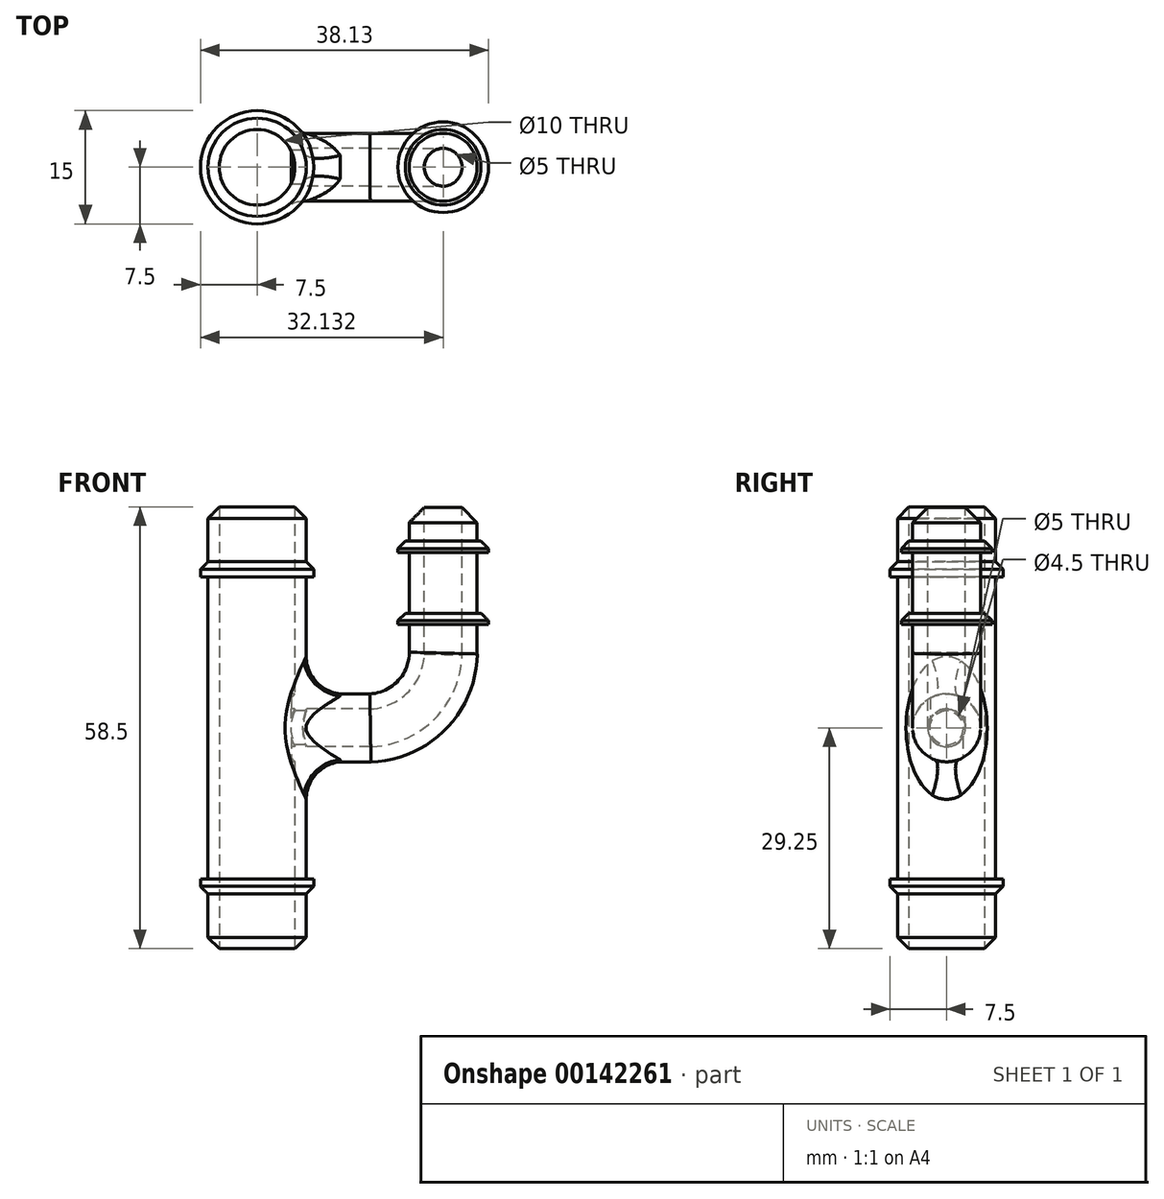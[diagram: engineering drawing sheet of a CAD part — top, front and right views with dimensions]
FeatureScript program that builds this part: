
annotation { "Feature Type Name" : "Feature", "Feature Type Description" : "" }
export const myFeature = defineFeature(function(context is Context, id is Id, definition is map)
    precondition{}
    {
        {
            var Q0;
            Q0=qCreatedBy(makeId("Front.planeOp"),FACE);
            var sketch = newSketch(context, id + "F0", { "sketchPlane" : qUnion([Q0])});
            skLineSegment(sketch, "E0.bottom", {"start": v(4.5, 4.5) * mm, "end": v(34.5, 4.5) * mm});
            skLineSegment(sketch, "E0.top", {"start": v(4.5, 2.5) * mm, "end": v(11, 2.5) * mm});
            skLineSegment(sketch, "E0.left", {"start": v(4.5, 4.5) * mm, "end": v(4.5, 2.5) * mm});
            skLineSegment(sketch, "E0.right", {"start": v(11, 4.5) * mm, "end": v(11, 2.5) * mm});
            skLineSegment(sketch, "E1", {"start": v(-36.5, 0) * mm, "end": v(54.36, 0) * mm, "construction": true});
            skLineSegment(sketch, "E2", {"start": v(0, 12.73) * mm, "end": v(0, -11.94) * mm, "construction": true});
            skSolve(sketch);
        }
        {
            var Q0;
            Q0=makeQuery(id+"F0.imprint","IMPRINT",FACE,{"disambiguationData":[TD([[makeQuery(id+"F0.imprint","IMPRINT",EDGE,{"derivedFrom":sQuery(id+"F0.wireOp",EDGE,"E0.bottom")}),-1.0]])]});
            var Q1;
            {var subQ0=sQuery(id+"F0.wireOp",EDGE,"a35777e7-ca00-45c0-8781-a7bbb4af3e560.MirrorCS");Q1=makeQuery(id+"F0.imprint","IMPRINT",FACE,{"disambiguationData":[TD([[makeQuery(id+"F0.imprint","IMPRINT",EDGE,{"derivedFrom":subQ0}),-1.0]])]});}
            var Q2;
            Q2=makeQuery(id+"F0.imprint","IMPRINT",FACE,{"disambiguationData":[TD([[makeQuery(id+"F0.imprint","IMPRINT",EDGE,{"derivedFrom":sQuery(id+"F0.wireOp",EDGE,"mlNMObRF-hjKZ-VAvK-cDcy-euMoUcQcRU43.bottom")}),-1.0]])]});
            var Q3;
            Q3=sQuery(id+"F0.wireOp",EDGE,"E1");
            revolve(context, id + "F1", {"entities" : qUnion([Q0, Q1, Q2]), "axis" : qUnion([Q3]), "revolveType" : RevolveType.FULL});
        }
        {
            var Q0;
            Q0=qCreatedBy(makeId("Top.planeOp"),FACE);
            var sketch = newSketch(context, id + "F2", { "sketchPlane" : qUnion([Q0])});
            skCircle(sketch, "E3", {"center": v(0, 0) * mm, "radius": 6.5 * mm});
            skCircle(sketch, "E4", {"center": v(0, 0) * mm, "radius": 5 * mm});
            skSolve(sketch);
        }
        {
            var Q0;
            Q0=makeQuery(id+"F2.imprint","IMPRINT",FACE,{"disambiguationData":[TD([[makeQuery(id+"F2.imprint","IMPRINT",EDGE,{"derivedFrom":sQuery(id+"F2.wireOp",EDGE,"E3")}),1.0]])]});
            extrude(context, id + "F3", {"entities" : qUnion([Q0]), "operationType" : NewBodyOperationType.ADD, "endBound" : BoundingType.SYMMETRIC, "depth" : 61.5 * mm});
        }
        {
            var Q0;
            Q0=makeQuery(id+"F3.opExtrude","CAP_EDGE",EDGE,{"disambiguationData":[OSD([sQuery(id+"F2.wireOp",EDGE,"E3")])],"isStart":false});
            var Q1;
            Q1=makeQuery(id+"F3.opExtrude","CAP_EDGE",EDGE,{"disambiguationData":[OSD([sQuery(id+"F2.wireOp",EDGE,"E3")])],"isStart":true});
            chamfer(context, id + "F4", {"entities" : qUnion([Q0, Q1]), "width" : 3 * mm, "tangentPropagation" : true});
        }
        {
            var Q0;
            {var subQ0=sQuery(id+"F0.wireOp",EDGE,"E0.bottom");Q0=makeQuery(id+"F3.boolean.opBoolean","INTERSECT",EDGE,{"derivedFrom":[makeQuery(id+"F1.opRevolve","SWEPT_FACE",FACE,{"disambiguationData":[OSD([subQ0]),TDD([makeQuery(id+"F0.imprint","IMPRINT",EDGE,{"disambiguationData":[TD([[makeQuery(id+"F0.imprint","INTERSECT",VERTEX,{"derivedFrom":[subQ0,sQuery(id+"F0.wireOp",EDGE,"E0.left")]}),-1.0]])],"derivedFrom":subQ0})])]}),makeQuery(id+"F3.opExtrude","SWEPT_FACE",FACE,{"disambiguationData":[OSD([sQuery(id+"F2.wireOp",EDGE,"E3")])]})]});}
            fillet(context, id + "F5", {"entities" : qUnion([Q0]), "radius" : 5 * mm, "tangentPropagation" : true, "allowEdgeOverflow" : false});
        }
        {
            var Q0;
            Q0=qCreatedBy(makeId("Front.planeOp"),FACE);
            var sketch = newSketch(context, id + "F6", { "sketchPlane" : qUnion([Q0])});
            skLineSegment(sketch, "E5", {"start": v(0, 31.28) * mm, "end": v(0, -33.3) * mm, "construction": true});
            skLineSegment(sketch, "E6.bottom", {"start": v(-7.5, 22) * mm, "end": v(-5.5, 22) * mm});
            skLineSegment(sketch, "E6.top", {"start": v(-7.5, 20) * mm, "end": v(-5.5, 20) * mm});
            skLineSegment(sketch, "E6.left", {"start": v(-7.5, 22) * mm, "end": v(-7.5, 20) * mm});
            skLineSegment(sketch, "E6.right", {"start": v(-5.5, 22) * mm, "end": v(-5.5, 20) * mm});
            skLineSegment(sketch, "E7", {"start": v(-17.18, 0) * mm, "end": v(34.4, 0) * mm, "construction": true});
            skLineSegment(sketch, "E8.MirrorCS", {"start": v(-7.5, -22) * mm, "end": v(-7.5, -20) * mm});
            skLineSegment(sketch, "E9.MirrorCS", {"start": v(-7.5, -22) * mm, "end": v(-5.5, -22) * mm});
            skLineSegment(sketch, "E10.MirrorCS", {"start": v(-5.5, -22) * mm, "end": v(-5.5, -20) * mm});
            skLineSegment(sketch, "E11.MirrorCS", {"start": v(-7.5, -20) * mm, "end": v(-5.5, -20) * mm});
            skSolve(sketch);
        }
        {
            var Q0;
            Q0=makeQuery(id+"F6.imprint","IMPRINT",FACE,{"disambiguationData":[TD([[makeQuery(id+"F6.imprint","IMPRINT",EDGE,{"derivedFrom":sQuery(id+"F6.wireOp",EDGE,"E6.bottom")}),-1.0]])]});
            var Q1;
            Q1=makeQuery(id+"F6.imprint","IMPRINT",FACE,{"disambiguationData":[TD([[makeQuery(id+"F6.imprint","IMPRINT",EDGE,{"derivedFrom":sQuery(id+"F6.wireOp",EDGE,"E8.MirrorCS")}),-1.0]])]});
            var Q2;
            Q2=sQuery(id+"F6.wireOp",EDGE,"E5");
            revolve(context, id + "F7", {"operationType" : NewBodyOperationType.ADD, "entities" : qUnion([Q0, Q1]), "axis" : qUnion([Q2]), "revolveType" : RevolveType.FULL});
        }
        {
            var Q0;
            Q0=makeQuery(id+"F7.opRevolve","SWEPT_EDGE",EDGE,{"disambiguationData":[OSD([sQuery(id+"F6.wireOp",EDGE,"E8.MirrorCS"),sQuery(id+"F6.wireOp",EDGE,"E9.MirrorCS")])]});
            var Q1;
            Q1=makeQuery(id+"F7.opRevolve","SWEPT_EDGE",EDGE,{"disambiguationData":[OSD([sQuery(id+"F6.wireOp",EDGE,"E6.bottom"),sQuery(id+"F6.wireOp",EDGE,"E6.left")])]});
            chamfer(context, id + "F8", {"entities" : qUnion([Q0, Q1]), "width" : 1 * mm, "tangentPropagation" : true});
        }
        {
            var Q0;
            Q0=qCreatedBy(makeId("Right.planeOp"),FACE);
            var sketch = newSketch(context, id + "F9", { "sketchPlane" : qUnion([Q0])});
            skCircle(sketch, "E12", {"center": v(0, 0) * mm, "radius": 2.25 * mm});
            skSolve(sketch);
        }
        {
            var Q0;
            Q0=makeQuery(id+"F9.imprint","IMPRINT",FACE,{"disambiguationData":[TD([[makeQuery(id+"F9.imprint","IMPRINT",EDGE,{"derivedFrom":sQuery(id+"F9.wireOp",EDGE,"E12")}),1.0]])]});
            extrude(context, id + "F10", {"entities" : qUnion([Q0]), "operationType" : NewBodyOperationType.REMOVE, "depth" : 10 * mm});
        }
        {
            var Q0;
            Q0=qCreatedBy(makeId("Front.planeOp"),FACE);
            var sketch = newSketch(context, id + "F11", { "sketchPlane" : qUnion([Q0])});
            skLineSegment(sketch, "E13", {"start": v(11.05, 0) * mm, "end": v(15, 0) * mm});
            skLineSegment(sketch, "E14", {"start": v(24.63, 9.73) * mm, "end": v(24.63, 29.73) * mm});
            skArc(sketch, "E15", {"start": v(15, 0) * mm, "mid": v(21.74, 2.96) * mm, "end": v(24.63, 9.73) * mm});
            skLineSegment(sketch, "E16.bottom", {"start": v(18.63, 24.73) * mm, "end": v(20.13, 24.73) * mm});
            skLineSegment(sketch, "E16.top", {"start": v(18.63, 23.23) * mm, "end": v(20.13, 23.23) * mm});
            skLineSegment(sketch, "E16.left", {"start": v(18.63, 24.73) * mm, "end": v(18.63, 23.23) * mm});
            skLineSegment(sketch, "E16.right", {"start": v(20.13, 24.73) * mm, "end": v(20.13, 23.23) * mm});
            skLineSegment(sketch, "E17", {"start": v(24.63, 9.73) * mm, "end": v(24.63, 33.76) * mm, "construction": true});
            skLineSegment(sketch, "E18", {"start": v(12.95, 19.2) * mm, "end": v(36.94, 19.2) * mm, "construction": true});
            skLineSegment(sketch, "E19.MirrorCS", {"start": v(18.63, 15.19) * mm, "end": v(20.13, 15.19) * mm});
            skLineSegment(sketch, "E20.MirrorCS", {"start": v(18.63, 13.69) * mm, "end": v(18.63, 15.19) * mm});
            skLineSegment(sketch, "E21.MirrorCS", {"start": v(20.13, 13.69) * mm, "end": v(20.13, 15.19) * mm});
            skLineSegment(sketch, "E22.MirrorCS", {"start": v(18.63, 13.69) * mm, "end": v(20.13, 13.69) * mm});
            skSolve(sketch);
        }
        {
            var Q0;
            Q0=makeQuery(id+"F1.opRevolve","SWEPT_FACE",FACE,{"disambiguationData":[OSD([sQuery(id+"F0.wireOp",EDGE,"E0.right")])]});
            var Q1;
            Q1=sQuery(id+"F11.wireOp",EDGE,"E13");
            var Q2;
            Q2=sQuery(id+"F11.wireOp",EDGE,"E15");
            var Q3;
            Q3=sQuery(id+"F11.wireOp",EDGE,"E14");
            sweep(context, id + "F12", {"operationType" : NewBodyOperationType.ADD, "profiles" : qUnion([Q0]), "path" : qUnion([Q1, Q2, Q3])});
        }
        {
            var Q0;
            Q0=makeQuery(id+"F12.opSweep","CAP_EDGE",EDGE,{"disambiguationData":[OSD([sQuery(id+"F0.wireOp",EDGE,"E0.bottom"),sQuery(id+"F0.wireOp",EDGE,"E0.right"),sQuery(id+"F11.wireOp",VERTEX,"E14.end")])],"isStart":false});
            chamfer(context, id + "F13", {"entities" : qUnion([Q0]), "width" : 2.5 * mm});
        }
        {
            var Q0;
            Q0=makeQuery(id+"F11.imprint","IMPRINT",FACE,{"disambiguationData":[TD([[makeQuery(id+"F11.imprint","IMPRINT",EDGE,{"derivedFrom":sQuery(id+"F11.wireOp",EDGE,"E16.bottom")}),-1.0]])]});
            var Q1;
            Q1=makeQuery(id+"F11.imprint","IMPRINT",FACE,{"disambiguationData":[TD([[makeQuery(id+"F11.imprint","IMPRINT",EDGE,{"derivedFrom":sQuery(id+"F11.wireOp",EDGE,"E19.MirrorCS")}),-1.0]])]});
            var Q2;
            Q2=sQuery(id+"F11.wireOp",EDGE,"E17");
            revolve(context, id + "F14", {"operationType" : NewBodyOperationType.ADD, "entities" : qUnion([Q0, Q1]), "axis" : qUnion([Q2]), "revolveType" : RevolveType.FULL});
        }
        {
            var Q0;
            Q0=makeQuery(id+"F14.opRevolve","SWEPT_EDGE",EDGE,{"disambiguationData":[OSD([sQuery(id+"F11.wireOp",EDGE,"E16.bottom"),sQuery(id+"F11.wireOp",EDGE,"E16.left")])]});
            var Q1;
            Q1=makeQuery(id+"F14.opRevolve","SWEPT_EDGE",EDGE,{"disambiguationData":[OSD([sQuery(id+"F11.wireOp",EDGE,"E19.MirrorCS"),sQuery(id+"F11.wireOp",EDGE,"E20.MirrorCS")])]});
            chamfer(context, id + "F15", {"entities" : qUnion([Q0, Q1]), "width" : 1 * mm, "tangentPropagation" : true});
        }
    });
